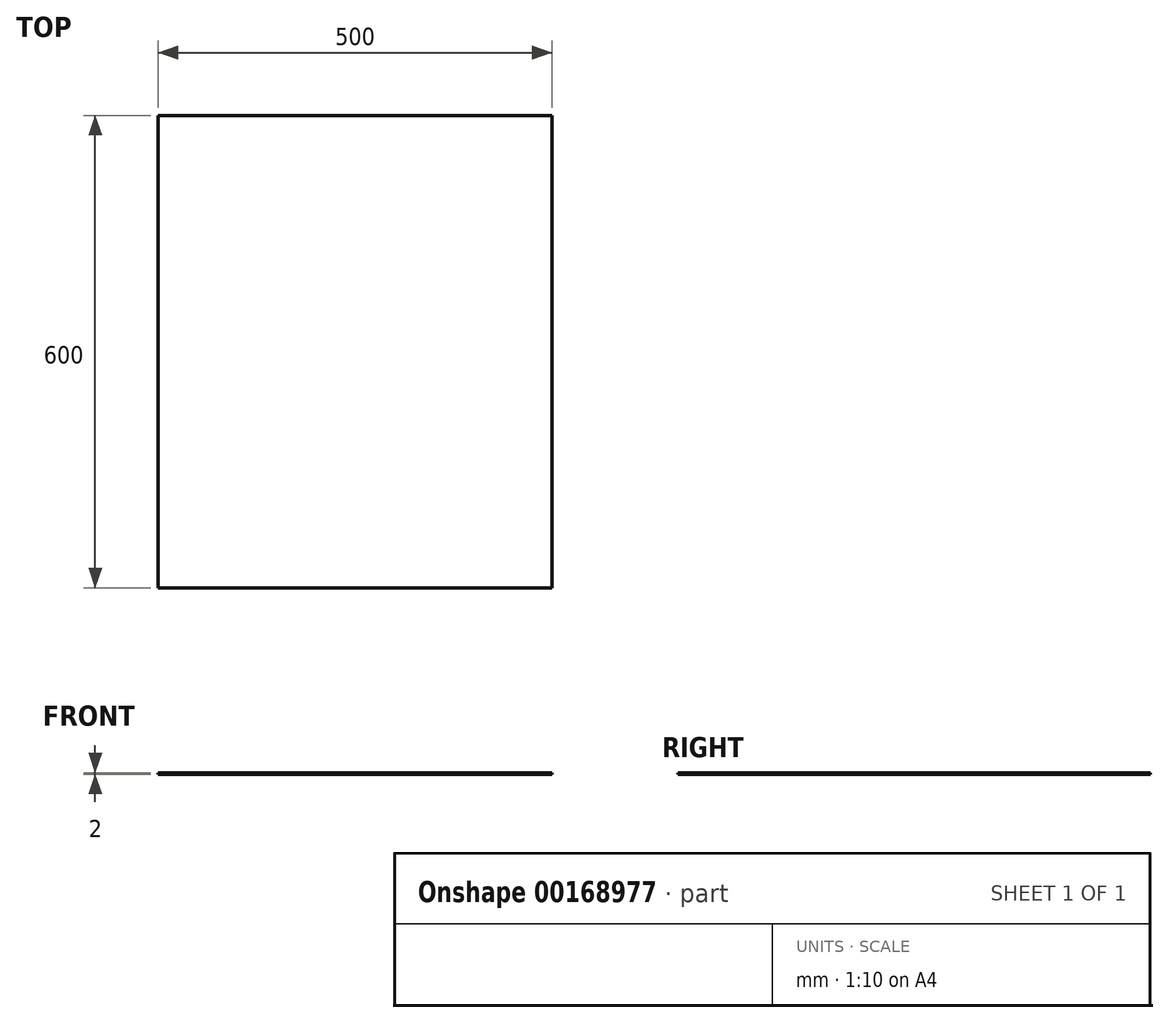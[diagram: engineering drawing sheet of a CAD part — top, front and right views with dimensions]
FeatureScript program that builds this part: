
annotation { "Feature Type Name" : "Feature", "Feature Type Description" : "" }
export const myFeature = defineFeature(function(context is Context, id is Id, definition is map)
    precondition{}
    {
        {
            var Q0;
            Q0=qCreatedBy(makeId("Top.planeOp"),FACE);
            var sketch = newSketch(context, id + "F0", { "sketchPlane" : qUnion([Q0])});
            skLineSegment(sketch, "E0.bottom", {"start": v(250, 300) * mm, "end": v(-250, 300) * mm});
            skLineSegment(sketch, "E0.top", {"start": v(250, -300) * mm, "end": v(-250, -300) * mm});
            skLineSegment(sketch, "E0.left", {"start": v(250, 300) * mm, "end": v(250, -300) * mm});
            skLineSegment(sketch, "E0.right", {"start": v(-250, 300) * mm, "end": v(-250, -300) * mm});
            skPoint(sketch, "E0.middle", {"position": v(0, 0) * mm});
            skSolve(sketch);
        }
        {
            var Q0;
            Q0=makeQuery(id+"F0.imprint","IMPRINT",FACE,{"disambiguationData":[TD([[makeQuery(id+"F0.imprint","IMPRINT",EDGE,{"derivedFrom":sQuery(id+"F0.wireOp",EDGE,"E0.bottom")}),1.0]])]});
            extrude(context, id + "F1", {"entities" : qUnion([Q0]), "depth" : 2 * mm});
        }
    });
